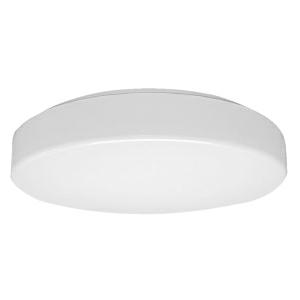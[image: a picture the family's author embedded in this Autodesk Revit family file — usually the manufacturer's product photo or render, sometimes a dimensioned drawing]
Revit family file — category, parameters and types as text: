
# Revit family: oblo_fit_-_oba_2000_830_d_00813350_cd9d
name_source: partatom
category: Lighting Fixtures
units: mm (PartAtom-declared; Revit-internal decimal feet)

## family parameters
Cut with Voids When Loaded = No
Host = Face
Light Source = No
Part Type = Normal
Room Calculation Point = No
Round Connector Dimension = Use Diameter
Shared = No

## types (1)
- OBLO.fit - OBA 2000/830/D (1 x LED, 2100 lm, 3000K)
    Apparent Load = 22 VA
    Approval mark = CE
    CIE Flux Codes = 41 72 91 84 100
    Color Rendering = 80-89
    Color Temperature = 3000K
    Control Gear = Electronic ballast
    Default Elevation = 1800 mm
    Description = OBA 2000/830/D|Surface-mounted luminaire.|light source:   Warm white   |work equipment: Power supply unit|luminous flux: 2100 lm|light distribution: Direct|class of protection: I|technology: Continuously dimmable|mains lead: Direct power supply|glare control: without|special features: DALI Load 1x|
    Frequency = 50 Hz, 60 Hz
    Height = 85 mm
    Lamp = 1 x LED
    Lamp Light Flux = 2100 lm
    Lamp count = 1
    Length = 370 mm
    Luminous efficacy = 95 lm/W
    Manufacturer = Waldmann
    ModVariant = No
    Model = 00813350
    Mounting Place = Ceiling
    Mounting Type = Surface mounted
    Number of Poles = 1
    OnlyDefault = Yes
    Power Factor = 1
    Product Name = OBLO.fit - OBA 2000/830/D
    Product group = Ceiling mounted luminaire
    ProductGroupID = 3
    Protection Class = Protection class I
    Protection Degree = IP 40
    RLX_Detail_Level = 1
    RLX_Emergency_Light_Flux = 0 lm
    RLX_Emergency_Type = 0
    RLX_Emergency_Type_DB = No
    RlxData = <blob elided: 22417 chars, md5=3129fd7b>
    Socket = socket
    Standby Power = 0 W
    System Light Flux = 2100 lm
    System Power = 22 W
    Type Comments = Product without accessories
    Type Image = oblo_led.jpg
    URL = http://relux.com
    VarID = ---
    Voltage = 230 V
    Voltage Range = 220-240 V
    Weight = 0.00 kg
    Width = 0 mm  [stored 0 ft]

note: [stored X ft] marks values corroborated as IEEE doubles in the binary element streams (Revit-internal decimal feet)

## geometry (parser evidence)
native form markers: Blend x4, Sweep x14
no freeform markers — native parametric forms only
